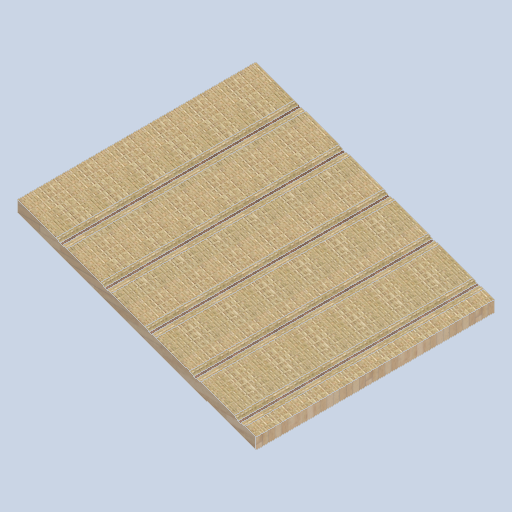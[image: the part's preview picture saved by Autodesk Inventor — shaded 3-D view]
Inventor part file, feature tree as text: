
AUTODESK INVENTOR PART (.ipt)
format: ipt  version: 2024.2 (Build 282272000, 272)  size: 353,792 bytes
history: native  units: in
note: dims shown in document units (in); Inventor stores cm internally (conversion verified against a paired STEP export)
features: other x3, sketch x3, plane x3
ambient origin geometry x8: Origin, YZ Plane, XZ Plane, XY Plane, X Axis, Y Axis, Z Axis, Center Point
bodies: Solid1 (feature_tree)
feature tree (9):
  other  "side_curve_panel_01.ipt"
  other  "Solid1::side_curve_panel_01.ipt"
  other  "TaggingFeature1"
  sketch  "Sketch1"  dims[d0=0.3937in]
  sketch  "Sketch4"
  sketch  "Sketch5"
  plane  "Work Plane1"
  plane  "Work Plane2"
  plane  "Work Plane3"
